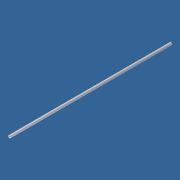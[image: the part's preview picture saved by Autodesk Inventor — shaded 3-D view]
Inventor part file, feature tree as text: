
AUTODESK INVENTOR PART (.ipt)
format: ipt  version: 2012 (Build 160160000, 160)  size: 81,920 bytes
history: native  units: in
note: dims shown in document units (in); Inventor stores cm internally (conversion verified against a paired STEP export)
features: extrude x2, sketch x2, plane x1, other x1, projected_geometry x1
ambient origin geometry x8: Origin, YZ Plane, XZ Plane, XY Plane, X Axis, Y Axis, Z Axis, Center Point
bodies: Solid1 (feature_tree)
feature tree (7):
  extrude  "Extrusion1"  Depth=1.04in
  plane  "Work Plane1"
  extrude  "Extrusion2"  TaperAngle=0.0deg  [1 undecoded]
  sketch  "Sketch1"  dims[d0=1.31in d1=1.04in]
  other  "Work Axis1"
  sketch  "Sketch2"  dims[d2=82.0in d3=0.0in d4=0.0in d10=1.4in d11=0.0in d13=0.3125in]
  projected_geometry  "Project Cut Edges1"
note: 1 required parameter value undecoded (feature->parameter linkage not recoverable at this tier; creation-order binding heuristic only, values carry confidence <= 0.55)
